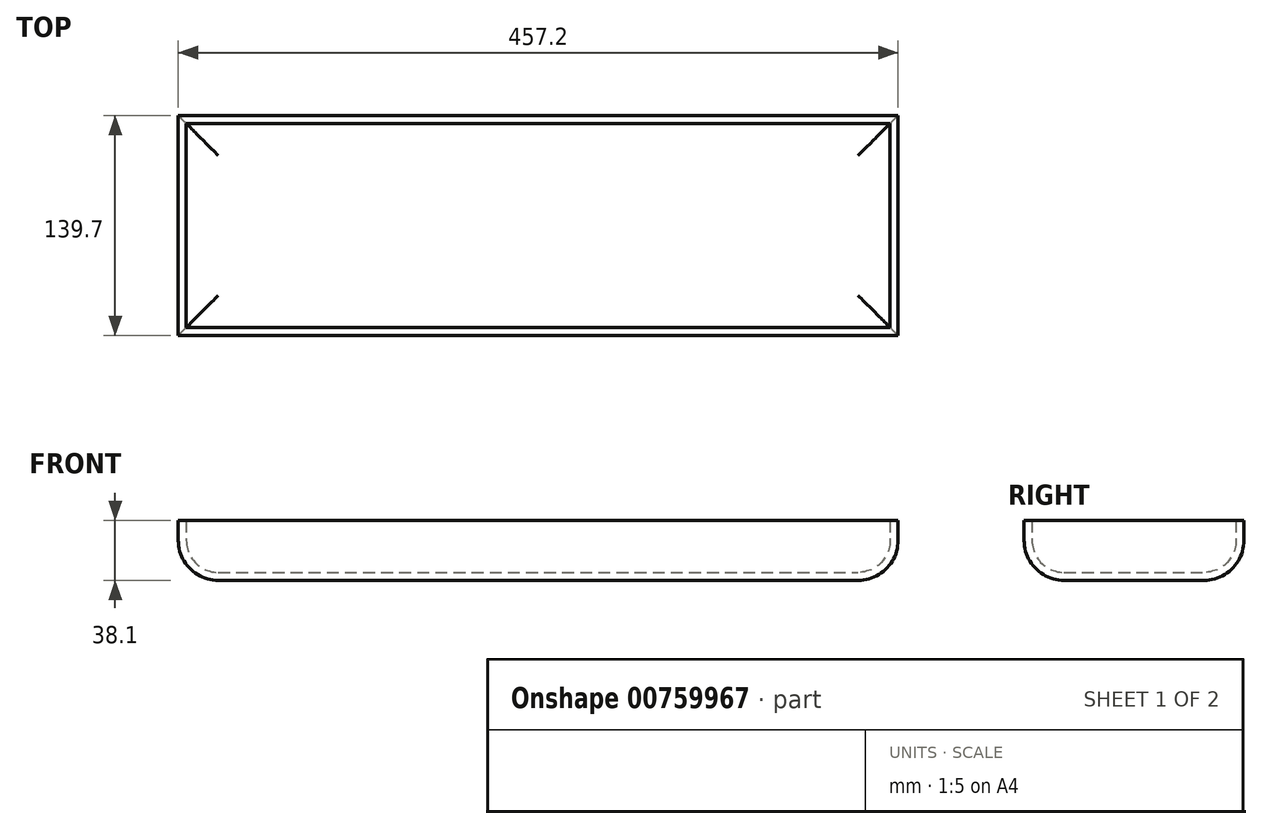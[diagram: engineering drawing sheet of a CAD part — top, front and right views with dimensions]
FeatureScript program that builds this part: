
annotation { "Feature Type Name" : "Feature", "Feature Type Description" : "" }
export const myFeature = defineFeature(function(context is Context, id is Id, definition is map)
    precondition{}
    {
        {
            var Q0;
            Q0=qCreatedBy(makeId("Top.planeOp"),FACE);
            var sketch = newSketch(context, id + "F0", { "sketchPlane" : qUnion([Q0])});
            skLineSegment(sketch, "E0.bottom", {"start": v(-228.6, 69.85) * mm, "end": v(228.6, 69.85) * mm});
            skLineSegment(sketch, "E0.top", {"start": v(-228.6, -69.85) * mm, "end": v(228.6, -69.85) * mm});
            skLineSegment(sketch, "E0.left", {"start": v(-228.6, 69.85) * mm, "end": v(-228.6, -69.85) * mm});
            skLineSegment(sketch, "E0.right", {"start": v(228.6, 69.85) * mm, "end": v(228.6, -69.85) * mm});
            skPoint(sketch, "E0.middle", {"position": v(0, 0) * mm});
            skSolve(sketch);
        }
        {
            var Q0;
            Q0 = qSketchRegion(id + "F0", true);
            extrude(context, id + "F1", {"entities" : qUnion([Q0]), "depth" : 38.1 * mm, "offsetDistance" : 25.4 * mm});
        }
        {
            var Q0;
            Q0=makeQuery(id+"F1.opExtrude","CAP_FACE",FACE,{"disambiguationData":[OSD([sQuery(id+"F0.wireOp",EDGE,"E0.bottom"),sQuery(id+"F0.wireOp",EDGE,"E0.top"),sQuery(id+"F0.wireOp",EDGE,"E0.left"),sQuery(id+"F0.wireOp",EDGE,"E0.right")])],"isStart":true});
            fillet(context, id + "F2", {"entities" : qUnion([Q0]), "radius" : 25.4 * mm, "tangentPropagation" : true, "allowEdgeOverflow" : false});
        }
        {
            var Q0;
            Q0=makeQuery(id+"F1.opExtrude","CAP_FACE",FACE,{"disambiguationData":[OSD([sQuery(id+"F0.wireOp",EDGE,"E0.bottom"),sQuery(id+"F0.wireOp",EDGE,"E0.top"),sQuery(id+"F0.wireOp",EDGE,"E0.left"),sQuery(id+"F0.wireOp",EDGE,"E0.right")])],"isStart":false});
            shell(context, id + "F3", {"entities" : qUnion([Q0]), "thickness" : 5.08 * mm});
        }
        {
            var Q0;
            Q0=qCreatedBy(makeId("Top.planeOp"),FACE);
            cPlane(context, id + "F4", {"entities" : qUnion([Q0]), "cplaneType" : CPlaneType.OFFSET, "offset" : 12.7 * mm, "oppositeDirection" : true, "width" : 152.4 * mm, "height" : 152.4 * mm});
        }
        {
            var Q0;
            Q0=qCreatedBy(id+"F4.planeOp",FACE);
            var sketch = newSketch(context, id + "F5", { "sketchPlane" : qUnion([Q0])});
            skLineSegment(sketch, "E1", {"start": v(-228.6, 0) * mm, "end": v(228.6, 0) * mm, "construction": true});
            skLineSegment(sketch, "E2", {"start": v(0, -69.85) * mm, "end": v(0, 69.85) * mm, "construction": true});
            skLineSegment(sketch, "E3.bottom", {"start": v(40.64, -30.48) * mm, "end": v(-218.44, -30.48) * mm});
            skLineSegment(sketch, "E3.top", {"start": v(40.64, 30.48) * mm, "end": v(-218.44, 30.48) * mm});
            skLineSegment(sketch, "E3.left", {"start": v(40.64, -30.48) * mm, "end": v(40.64, 30.48) * mm});
            skLineSegment(sketch, "E3.right", {"start": v(-218.44, -30.48) * mm, "end": v(-218.44, 30.48) * mm});
            skPoint(sketch, "E3.middle", {"position": v(-88.9, 0) * mm});
            skSolve(sketch);
        }
        {
            var Q0;
            Q0=qCreatedBy(makeId("Top.planeOp"),FACE);
            cPlane(context, id + "F6", {"entities" : qUnion([Q0]), "cplaneType" : CPlaneType.OFFSET, "offset" : 25.4 * mm, "width" : 152.4 * mm, "height" : 152.4 * mm});
        }
        {
            var Q0;
            Q0=qCreatedBy(id+"F6.planeOp",FACE);
            var sketch = newSketch(context, id + "F7", { "sketchPlane" : qUnion([Q0])});
            skLineSegment(sketch, "E4.bottom", {"start": v(-228.6, -69.85) * mm, "end": v(228.6, -69.85) * mm});
            skLineSegment(sketch, "E4.top", {"start": v(-228.6, 69.85) * mm, "end": v(228.6, 69.85) * mm});
            skLineSegment(sketch, "E4.left", {"start": v(-228.6, -69.85) * mm, "end": v(-228.6, 69.85) * mm});
            skLineSegment(sketch, "E4.right", {"start": v(228.6, -69.85) * mm, "end": v(228.6, 69.85) * mm});
            skSolve(sketch);
        }
    });
